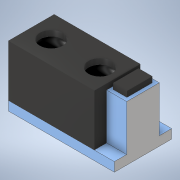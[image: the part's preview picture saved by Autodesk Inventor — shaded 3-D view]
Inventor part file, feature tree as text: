
AUTODESK INVENTOR PART (.ipt)
format: ipt  version: 2020 (Build 240168000, 168)  size: 222,720 bytes
history: native  units: mm
features: sketch x7, extrude x6, plane x4, other x1
ambient origin geometry x8: Origin, YZ Plane, XZ Plane, XY Plane, X Axis, Y Axis, Z Axis, Center Point
bodies: Solid2 (feature_tree)
feature tree (18):
  other  "Bryła1"
  extrude  "Wyciągnięcie proste1"  Depth=15.0mm
  extrude  "Wyciągnięcie proste2"  Depth=5.0mm
  extrude  "Wyciągnięcie proste3"  Depth=8.0mm
  extrude  "Extrusion4"  Depth=4.0mm
  extrude  "Extrusion5"  Depth=3.5mm
  extrude  "Extrusion7"  Depth=4.0mm
  plane  "Work Plane1"
  plane  "Work Plane2"
  plane  "Work Plane3"
  plane  "Work Plane4"
  sketch  "Sketch9"  dims[d7=4.0mm d8=0.0mm d9=4.0mm d10=3.5mm d11=4.0mm d12=3.0mm d13=4.0mm d14=4.0mm d15=1.0mm d16=0.0mm d17=1.6mm d18=0.0mm d19=18.5mm d20=3.5mm d21=5.7mm d22=2.15mm d23=0.0mm d24=8.0mm d25=0.0mm d32=4.4mm d33=0.65mm d34=2.4mm d35=0.5mm d36=1.0mm d37=0.0mm d38=-2.0mm d45=-1.0mm d46=-1.0mm d47=0.4mm d48=0.0mm d49=1.0mm d50=3.054326mm d51=6.108652mm d53=3.0mm d86=-5.0mm d54=0.872665mm d55=0.872665mm d83=0.5mm d84=0.872665mm d85=0.5mm d87=0.872665mm d88=0.5mm d89=0.872665mm]
  sketch  "Szkic1"
  sketch  "Szkic2"
  sketch  "Szkic3"
  sketch  "Sketch4"  dims[d0=10.0mm d1=15.0mm]
  sketch  "Sketch5"  dims[d2=5.0mm d3=7.5mm]
  sketch  "Sketch7"  dims[d4=5.0mm d5=0.0mm d6=8.0mm]
